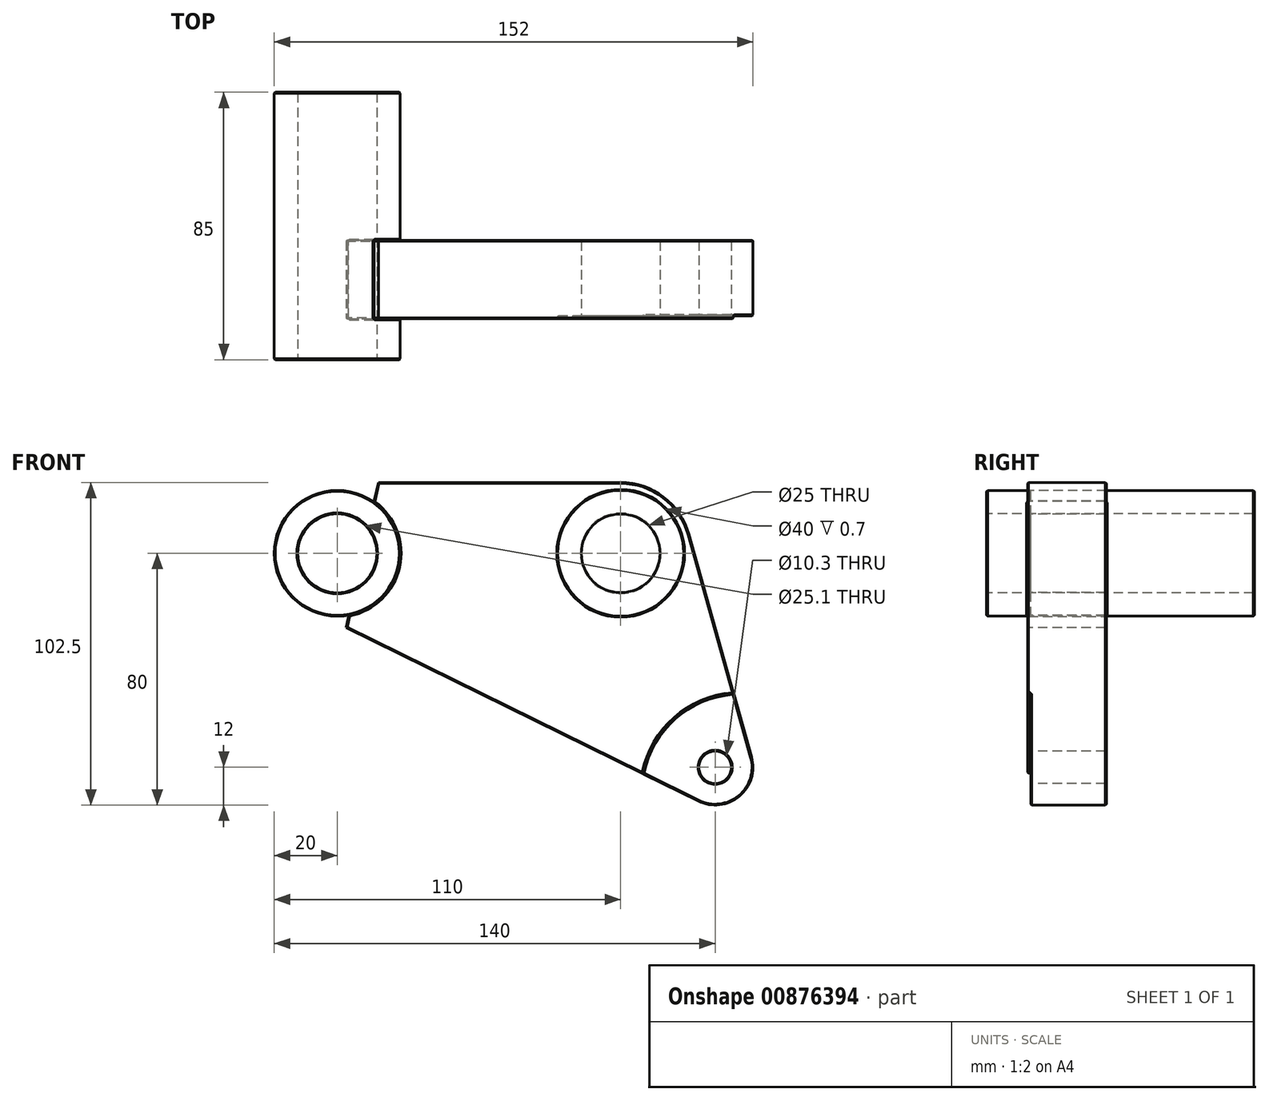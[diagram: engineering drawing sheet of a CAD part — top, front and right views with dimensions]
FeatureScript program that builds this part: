
annotation { "Feature Type Name" : "Feature", "Feature Type Description" : "" }
export const myFeature = defineFeature(function(context is Context, id is Id, definition is map)
    precondition{}
    {
        {
            var Q0;
            Q0=qCreatedBy(makeId("Front.planeOp"),FACE);
            var sketch = newSketch(context, id + "F0", { "sketchPlane" : qUnion([Q0])});
            skCircle(sketch, "E0", {"center": v(0, 0) * mm, "radius": 12.5 * mm});
            skCircle(sketch, "E1", {"center": v(0, 0) * mm, "radius": 20 * mm});
            skArc(sketch, "E2", {"start": v(21.66, 6.08) * mm, "mid": v(13.6, 17.93) * mm, "end": v(0, 22.5) * mm});
            skArc(sketch, "E3", {"start": v(24.7, -78.77) * mm, "mid": v(37.67, -77.23) * mm, "end": v(41.55, -64.76) * mm});
            skCircle(sketch, "E4", {"center": v(-90, 0) * mm, "radius": 20 * mm});
            skCircle(sketch, "E5", {"center": v(-90, 0) * mm, "radius": 12.55 * mm});
            skLineSegment(sketch, "E6", {"start": v(21.66, 6.08) * mm, "end": v(41.55, -64.76) * mm});
            skLineSegment(sketch, "E7", {"start": v(0, 22.5) * mm, "end": v(-76.95, 22.5) * mm});
            skLineSegment(sketch, "E8", {"start": v(-76.95, 22.5) * mm, "end": v(-87.2, -23.68) * mm});
            skLineSegment(sketch, "E9", {"start": v(-87.2, -23.68) * mm, "end": v(24.7, -78.77) * mm});
            skPoint(sketch, "E10", {"position": v(38, -76) * mm});
            skArc(sketch, "E11", {"start": v(7.06, -70.08) * mm, "mid": v(17.12, -52.41) * mm, "end": v(35.89, -44.57) * mm});
            skSolve(sketch);
        }
        {
            var Q0;
            Q0=makeQuery(id+"F0.imprint","IMPRINT",FACE,{"disambiguationData":[TD([[makeQuery(id+"F0.imprint","IMPRINT",EDGE,{"derivedFrom":sQuery(id+"F0.wireOp",EDGE,"E1")}),-1.0]])]});
            var Q1;
            Q1=makeQuery(id+"F0.imprint","IMPRINT",FACE,{"disambiguationData":[TD([[makeQuery(id+"F0.imprint","IMPRINT",EDGE,{"derivedFrom":sQuery(id+"F0.wireOp",EDGE,"E0")}),-1.0]])]});
            var Q2;
            {var subQ0=sQuery(id+"F0.wireOp",EDGE,"E3");Q2=makeQuery(id+"F0.imprint","IMPRINT",FACE,{"disambiguationData":[TD([[makeQuery(id+"F0.imprint","IMPRINT",EDGE,{"derivedFrom":subQ0}),1.0]])]});}
            extrude(context, id + "F1", {"entities" : qUnion([Q0, Q1, Q2]), "oppositeDirection" : true, "depth" : 25 * mm, "offsetDistance" : 25 * mm});
        }
        {
            var Q0;
            Q0=makeQuery(id+"F0.imprint","IMPRINT",FACE,{"disambiguationData":[TD([[makeQuery(id+"F0.imprint","IMPRINT",EDGE,{"derivedFrom":sQuery(id+"F0.wireOp",EDGE,"E0")}),-1.0]])]});
            var Q1;
            {var subQ0=sQuery(id+"F0.wireOp",EDGE,"E3");Q1=makeQuery(id+"F0.imprint","IMPRINT",FACE,{"disambiguationData":[TD([[makeQuery(id+"F0.imprint","IMPRINT",EDGE,{"derivedFrom":subQ0}),1.0]])]});}
            extrude(context, id + "F2", {"entities" : qUnion([Q0, Q1]), "operationType" : NewBodyOperationType.REMOVE, "oppositeDirection" : true, "depth" : 1 * mm, "offsetDistance" : 25 * mm});
        }
        {
            var Q0;
            Q0=sQuery(id+"F0.wireOp",VERTEX,"E3.center");
            var Q1;
            Q1=makeQuery(id+"F1.opExtrude","SWEPT_BODY",BODY,{"disambiguationData":[OSD([sQuery(id+"F0.wireOp",EDGE,"E0"),sQuery(id+"F0.wireOp",EDGE,"E2"),sQuery(id+"F0.wireOp",EDGE,"E3"),sQuery(id+"F0.wireOp",EDGE,"E4"),sQuery(id+"F0.wireOp",EDGE,"E6"),sQuery(id+"F0.wireOp",EDGE,"E7"),sQuery(id+"F0.wireOp",EDGE,"E8"),sQuery(id+"F0.wireOp",EDGE,"E9")])]});
            hole(context, id + "F3", {"style" : HoleStyle.SIMPLE, "endStyle" : HoleEndStyle.THROUGH, "standardTappedOrClearance" : lookupTablePath({ "standard" : "ISO", "engagement" : "75%", "pitch" : "1.75 mm", "size" : "M12", "type" : "Tapped" }), "standardBlindInLast" : lookupTablePath({ "standard" : "ISO", "engagement" : "75%", "pitch" : "1.75 mm", "size" : "M12", "type" : "Tapped" }), "holeDiameter" : 10.3 * mm, "majorDiameter" : 12 * mm, "showTappedDepth" : true, "isTappedThrough" : true, "tappedDepth" : 7.9 * mm, "tapClearance" : 3, "startFromSketch" : true, "locations" : qUnion([Q0]), "scope" : qUnion([Q1])});
        }
        {
            var Q0;
            {var subQ0=sQuery(id+"F0.wireOp",EDGE,"E8");var subQ1=sQuery(id+"F0.wireOp",EDGE,"E4");var subQ2=makeQuery(id+"F0.imprint","INTERSECT",VERTEX,{"disambiguationData":[OD(0.0)],"derivedFrom":[subQ1,subQ0]});Q0=makeQuery(id+"F0.imprint","IMPRINT",FACE,{"disambiguationData":[TD([[makeQuery(id+"F0.imprint","IMPRINT",EDGE,{"disambiguationData":[TD([[subQ2,1.0]])],"derivedFrom":subQ1}),1.0]])]});}
            var Q1;
            {var subQ0=sQuery(id+"F0.wireOp",EDGE,"E8");var subQ1=sQuery(id+"F0.wireOp",EDGE,"E4");var subQ2=makeQuery(id+"F0.imprint","INTERSECT",VERTEX,{"disambiguationData":[OD(0.0)],"derivedFrom":[subQ1,subQ0]});Q1=makeQuery(id+"F0.imprint","IMPRINT",FACE,{"disambiguationData":[TD([[makeQuery(id+"F0.imprint","IMPRINT",EDGE,{"disambiguationData":[TD([[subQ2,-1.0]])],"derivedFrom":subQ1}),1.0]])]});}
            extrude(context, id + "F4", {"entities" : qUnion([Q0, Q1]), "operationType" : NewBodyOperationType.ADD, "oppositeDirection" : true, "depth" : (85 - 13) * mm, "offsetDistance" : 25 * mm, "hasSecondDirection" : true, "secondDirectionOppositeDirection" : false, "secondDirectionDepth" : 13 * mm});
        }
        {
            var Q0;
            Q0=makeQuery(id+"F4.opExtrude","CAP_FACE",FACE,{"disambiguationData":[OSD([sQuery(id+"F0.wireOp",EDGE,"E4"),sQuery(id+"F0.wireOp",EDGE,"E5")])],"isStart":false});
            var Q1;
            Q1=makeQuery(id+"F1.opExtrude","CAP_FACE",FACE,{"disambiguationData":[OSD([sQuery(id+"F0.wireOp",EDGE,"E0"),sQuery(id+"F0.wireOp",EDGE,"E2"),sQuery(id+"F0.wireOp",EDGE,"E3"),sQuery(id+"F0.wireOp",EDGE,"E4"),sQuery(id+"F0.wireOp",EDGE,"E6"),sQuery(id+"F0.wireOp",EDGE,"E7"),sQuery(id+"F0.wireOp",EDGE,"E8"),sQuery(id+"F0.wireOp",EDGE,"E9")])],"isStart":false});
            var Q2;
            Q2=makeQuery(id+"F4.opExtrude","CAP_FACE",FACE,{"disambiguationData":[OSD([sQuery(id+"F0.wireOp",EDGE,"E4"),sQuery(id+"F0.wireOp",EDGE,"E5")])],"isStart":true});
            var Q3;
            Q3=makeQuery(id+"F1.opExtrude","CAP_FACE",FACE,{"disambiguationData":[OSD([sQuery(id+"F0.wireOp",EDGE,"E0"),sQuery(id+"F0.wireOp",EDGE,"E2"),sQuery(id+"F0.wireOp",EDGE,"E3"),sQuery(id+"F0.wireOp",EDGE,"E4"),sQuery(id+"F0.wireOp",EDGE,"E6"),sQuery(id+"F0.wireOp",EDGE,"E7"),sQuery(id+"F0.wireOp",EDGE,"E8"),sQuery(id+"F0.wireOp",EDGE,"E9")])],"isStart":true});
            var Q4;
            Q4=makeQuery(id+"F2.boolean.opBoolean","COPY",FACE,{"derivedFrom":makeQuery(id+"F2.opExtrude","CAP_FACE",FACE,{"disambiguationData":[OSD([sQuery(id+"F0.wireOp",EDGE,"E3"),sQuery(id+"F0.wireOp",EDGE,"E6"),sQuery(id+"F0.wireOp",EDGE,"E9"),sQuery(id+"F0.wireOp",EDGE,"E11")])],"isStart":false})});
            chamfer(context, id + "F5", {"entities" : qUnion([Q0, Q1, Q2, Q3, Q4]), "width" : 0.3 * mm, "tangentPropagation" : true});
        }
    });
